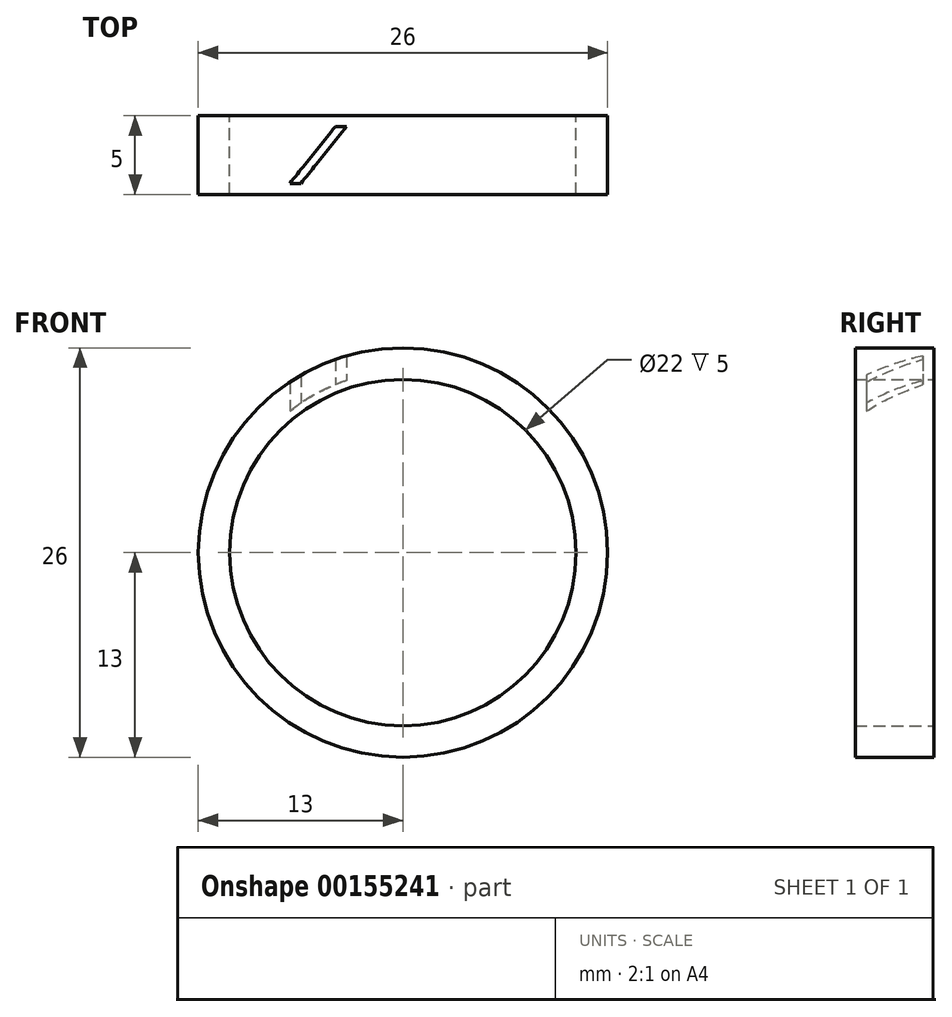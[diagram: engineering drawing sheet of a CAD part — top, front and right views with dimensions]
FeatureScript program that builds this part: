
annotation { "Feature Type Name" : "Feature", "Feature Type Description" : "" }
export const myFeature = defineFeature(function(context is Context, id is Id, definition is map)
    precondition{}
    {
        {
            var Q0;
            Q0=qCreatedBy(makeId("Front.planeOp"),FACE);
            var sketch = newSketch(context, id + "F0", { "sketchPlane" : qUnion([Q0])});
            skCircle(sketch, "E0", {"center": v(0, 0) * mm, "radius": 11 * mm});
            skCircle(sketch, "E1", {"center": v(0, 0) * mm, "radius": 13 * mm});
            skSolve(sketch);
        }
        {
            var Q0;
            Q0=makeQuery(id+"F0.imprint","IMPRINT",FACE,{"disambiguationData":[TD([[makeQuery(id+"F0.imprint","IMPRINT",EDGE,{"derivedFrom":sQuery(id+"F0.wireOp",EDGE,"E0")}),-1.0]])]});
            extrude(context, id + "F1", {"entities" : qUnion([Q0]), "depth" : 5 * mm});
        }
        {
            var Q0;
            Q0=qCreatedBy(makeId("Top.planeOp"),FACE);
            var sketch = newSketch(context, id + "F2", { "sketchPlane" : qUnion([Q0])});
            skLineSegment(sketch, "E2", {"start": v(0, 0) * mm, "end": v(0, -5) * mm});
            skLineSegment(sketch, "E3", {"start": v(-7.18, 0) * mm, "end": v(-7.18, -0.7) * mm});
            skLineSegment(sketch, "E4", {"start": v(-7.18, -5) * mm, "end": v(-7.18, -4.3) * mm});
            skLineSegment(sketch, "E5", {"start": v(0, -0.7) * mm, "end": v(0, -4.3) * mm});
            skLineSegment(sketch, "E6", {"start": v(-7.18, -4.3) * mm, "end": v(-4.3, -0.7) * mm});
            skLineSegment(sketch, "E7", {"start": v(-4.3, -0.7) * mm, "end": v(-3.6, -0.7) * mm});
            skLineSegment(sketch, "E8", {"start": v(-3.6, -0.7) * mm, "end": v(-6.48, -4.3) * mm});
            skLineSegment(sketch, "E9", {"start": v(-6.48, -4.3) * mm, "end": v(-7.18, -4.3) * mm});
            skSolve(sketch);
        }
        {
            var Q0;
            Q0 = qSketchRegion(id + "F2", true);
            extrude(context, id + "F3", {"entities" : qUnion([Q0]), "operationType" : NewBodyOperationType.REMOVE, "depth" : 25 * mm});
        }
        {
            var Q0;
            Q0=qCreatedBy(makeId("Front.planeOp"),FACE);
            var sketch = newSketch(context, id + "F4", { "sketchPlane" : qUnion([Q0])});
            skCircle(sketch, "E10", {"center": v(0, 0) * mm, "radius": 11.5 * mm});
            skCircle(sketch, "E11", {"center": v(0, 0) * mm, "radius": 11 * mm});
            skSolve(sketch);
        }
        {
            var Q0;
            Q0 = qSketchRegion(id + "F4", true);
            extrude(context, id + "F5", {"entities" : qUnion([Q0]), "operationType" : NewBodyOperationType.ADD, "depth" : 5 * mm});
        }
    });
